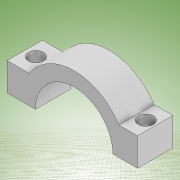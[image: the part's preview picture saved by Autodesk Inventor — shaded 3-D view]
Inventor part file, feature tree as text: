
AUTODESK INVENTOR PART (.ipt)
format: ipt  version: 2022 (Build 260153000, 153)  size: 137,728 bytes
history: native  units: mm
features: extrude x2, sketch x2, other x1
ambient origin geometry x8: Origin, YZ Plane, XZ Plane, XY Plane, X Axis, Y Axis, Z Axis, Center Point
bodies: Body1 (feature_tree)
feature tree (5):
  other  "Sólido1"
  extrude  "Extrusión1"  Depth=37.0mm
  extrude  "Extrusión2"  Depth=8.0mm
  sketch  "Boceto1"  dims[d0=11.0mm d1=37.0mm]
  sketch  "Boceto2"  dims[d2=8.0mm d3=8.0mm d5=4.0mm d6=10.0mm d7=0.0mm d8=4.3mm d9=4.3mm d10=0.0mm d11=0.0mm]
